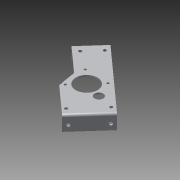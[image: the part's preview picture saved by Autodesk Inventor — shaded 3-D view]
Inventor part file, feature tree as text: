
AUTODESK INVENTOR PART (.ipt)
format: ipt  version: 2013 (Build 170138000, 138)  size: 392,192 bytes
history: native  units: in
note: dims shown in document units (in); Inventor stores cm internally (conversion verified against a paired STEP export)
features: other x15, sketch x14, sheet_metal_op x13, reference x1, extrude x1
ambient origin geometry x8: Origin, YZ Plane, XZ Plane, XY Plane, X Axis, Y Axis, Z Axis, Center Point
feature tree (44):
  sheet_metal_op  "Face2"
  sheet_metal_op  "Face5"
  sheet_metal_op  "Face6"
  sheet_metal_op  "Face7"
  sheet_metal_op  "Flange4"
  sheet_metal_op  "Flange5"
  sketch  "Sketch1"  dims[d8=0.125in]
  other  "Plate3"
  sketch  "Sketch8"  dims[d19=1.875in d20=0.375in d21=0.375in d22=0.375in d23=1.125in d24=1.6742in d25=1.6742in d26=1.8904in d27=0.3in d28=0.3in d29=0.3in d30=0.3in d31=0.125in]
  sketch  "Sketch9"  dims[d32=1.0in]
  other  "Plate8"
  sheet_metal_op  "Bend6"
  sketch  "Sketch10"  dims[d33=1.25in]
  sketch  "Sketch11"  dims[d86=2.0in]
  other  "Plate9"
  sheet_metal_op  "Bend7"
  sketch  "Sketch12"  dims[d87=0.125in]
  sketch  "Sketch14"  dims[d88=0.0in]
  sketch  "Sketch15"  dims[d89=3.0in]
  other  "Plate10"
  sheet_metal_op  "Bend8"
  sketch  "Sketch16"  dims[d90=0.125in]
  other  "Plate11"
  sheet_metal_op  "Bend9"
  sheet_metal_op  "Corner4"
  sketch  "Sketch17"  dims[d91=0.125in]
  other  "Plate12"
  sheet_metal_op  "Bend10"
  sheet_metal_op  "Corner5"
  sketch  "Sketch18"  dims[d92=0.0625in]
  sketch  "Sketch19"  dims[d93=0.25in]
  sketch  "Sketch20"  dims[d94=0.125in]
  reference  "Reference4"
  sketch  "Sketch21"  dims[d95=0.266in d96=0.266in d97=2.75in d98=0.3125in d99=0.5in d100=0.5in d101=0.125in d102=0.0in d103=3.875in d104=2.375in d105=0.125in d106=0.125in d107=0.0625in d108=0.25in d109=0.125in d110=0.266in d111=0.266in d112=0.5in d113=0.375in d114=1.5in d115=0.5in d116=0.125in d117=0.0in d124=0.0625in d126=0.125in d127=0.0in d128=0.2in d130=0.2in d131=0.2in d132=0.125in d133=0.125in d134=0.0625in d135=0.25in d136=0.125in d137=0.125in d138=0.0625in d139=0.25in d140=0.125in d141=1.25in d142=90.0deg d143=0.05in d144=0.5in d145=0.125in d146=0.125in d147=0.125in d148=0.0625in d149=0.25in d150=0.125in d151=1.25in d152=90.0deg d153=0.05in d154=0.5in d155=0.125in d156=0.125in d157=0.266in d158=0.266in d159=0.5in d160=0.375in d161=0.375in d162=0.5in d163=100.0in d164=0.0in d165=0.266in d166=0.375in d167=0.5in d168=0.125in d169=0.0in d171=0.748in d172=1.0in d173=24.0in d174=0.125in d175=0.0in d176=1.75in d177=0.5in d178=1.0in d179=0.266in d180=0.266in d181=0.125in d182=0.0in d0=0.125in d1=0.0625in d2=0.25in d3=0.125in d5=0.125in d6=0.0625in d7=0.25in d9=0.0in d10=0.125in d11=0.0625in d12=0.25in d13=0.125in d14=0.25in d15=0.125in d16=0.0625in d17=0.125in d18=1.0in]
  other  "Cut2"
  other  "Cut3"
  other  "Cut4"
  other  "Cut6"
  other  "Cut7"
  other  "Cut8"
  other  "Cut9"
  other  "Cut10"
  other  "Definition1"
  extrude  "Extrusion1"  Depth=0.125in
